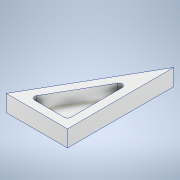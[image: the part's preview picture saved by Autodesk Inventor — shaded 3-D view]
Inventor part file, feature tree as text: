
AUTODESK INVENTOR PART (.ipt)
format: ipt  version: 2022 (Build 260153000, 153)  size: 119,296 bytes
history: native  units: mm
features: sketch x3, extrude x2, fillet x1, projected_geometry x1
ambient origin geometry x8: Origin, YZ Plane, XZ Plane, XY Plane, X Axis, Y Axis, Z Axis, Center Point
bodies: Solid1 (feature_tree)
feature tree (7):
  extrude  "Extrusion1"  Depth=147.8mm
  extrude  "Extrusion2"  Depth=20.0mm
  sketch  "Sketch3"  dims[d7=30.0deg d8=8.0mm]
  fillet  "Fillet1"  Radius=30.0mm
  sketch  "Sketch1"  dims[d0=256.0mm d1=147.8mm]
  sketch  "Sketch2"  dims[d2=40.0mm d3=0.0mm d4=20.0mm d5=30.0mm d6=0.0mm]
  projected_geometry  "Projected Loop1"
